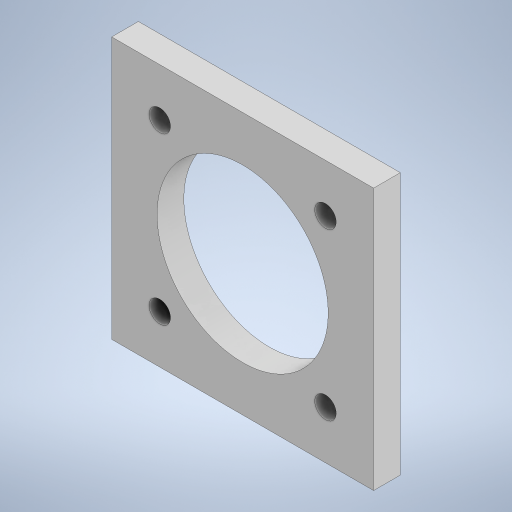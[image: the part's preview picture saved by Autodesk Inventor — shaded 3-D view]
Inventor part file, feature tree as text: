
AUTODESK INVENTOR PART (.ipt)
format: ipt  version: 2023 (Build 270158000, 158)  size: 231,424 bytes
history: native  units: mm
features: other x1, extrude x1, sketch x1
ambient origin geometry x8: Origin, YZ Plane, XZ Plane, XY Plane, X Axis, Y Axis, Z Axis, Center Point
bodies: Body1 (feature_tree)
feature tree (3):
  other  "Sólido1"
  extrude  "Extrusión1"  Depth=49.0mm
  sketch  "Boceto1"  dims[d0=49.0mm d1=49.0mm d2=4.0mm d3=9.0mm d4=40.0mm d6=360.0deg d8=5.0mm d9=0.0mm d10=32.0mm]
